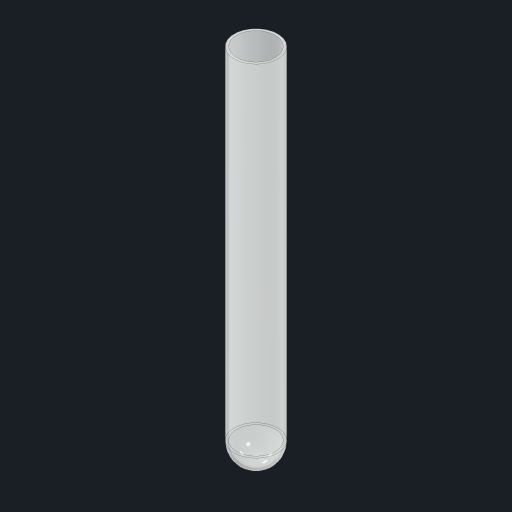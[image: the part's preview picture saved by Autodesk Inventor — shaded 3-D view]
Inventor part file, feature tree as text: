
AUTODESK INVENTOR PART (.ipt)
format: ipt  version: 2023.1 (Build 271208000, 208)  size: 95,744 bytes
history: native  units: in
note: dims shown in document units (in); Inventor stores cm internally (conversion verified against a paired STEP export)
features: revolve x1, sketch x1
ambient origin geometry x8: Origin, YZ Plane, XZ Plane, XY Plane, X Axis, Y Axis, Z Axis, Center Point
bodies: Solid1 (feature_tree)
feature tree (2):
  revolve  "Revolution1"  [1 undecoded]
  sketch  "Sketch1"  dims[d0=0.7087in d1=0.0394in d2=5.9055in d3=90.0deg]
note: 1 required parameter value undecoded (feature->parameter linkage not recoverable at this tier; creation-order binding heuristic only, values carry confidence <= 0.55)
